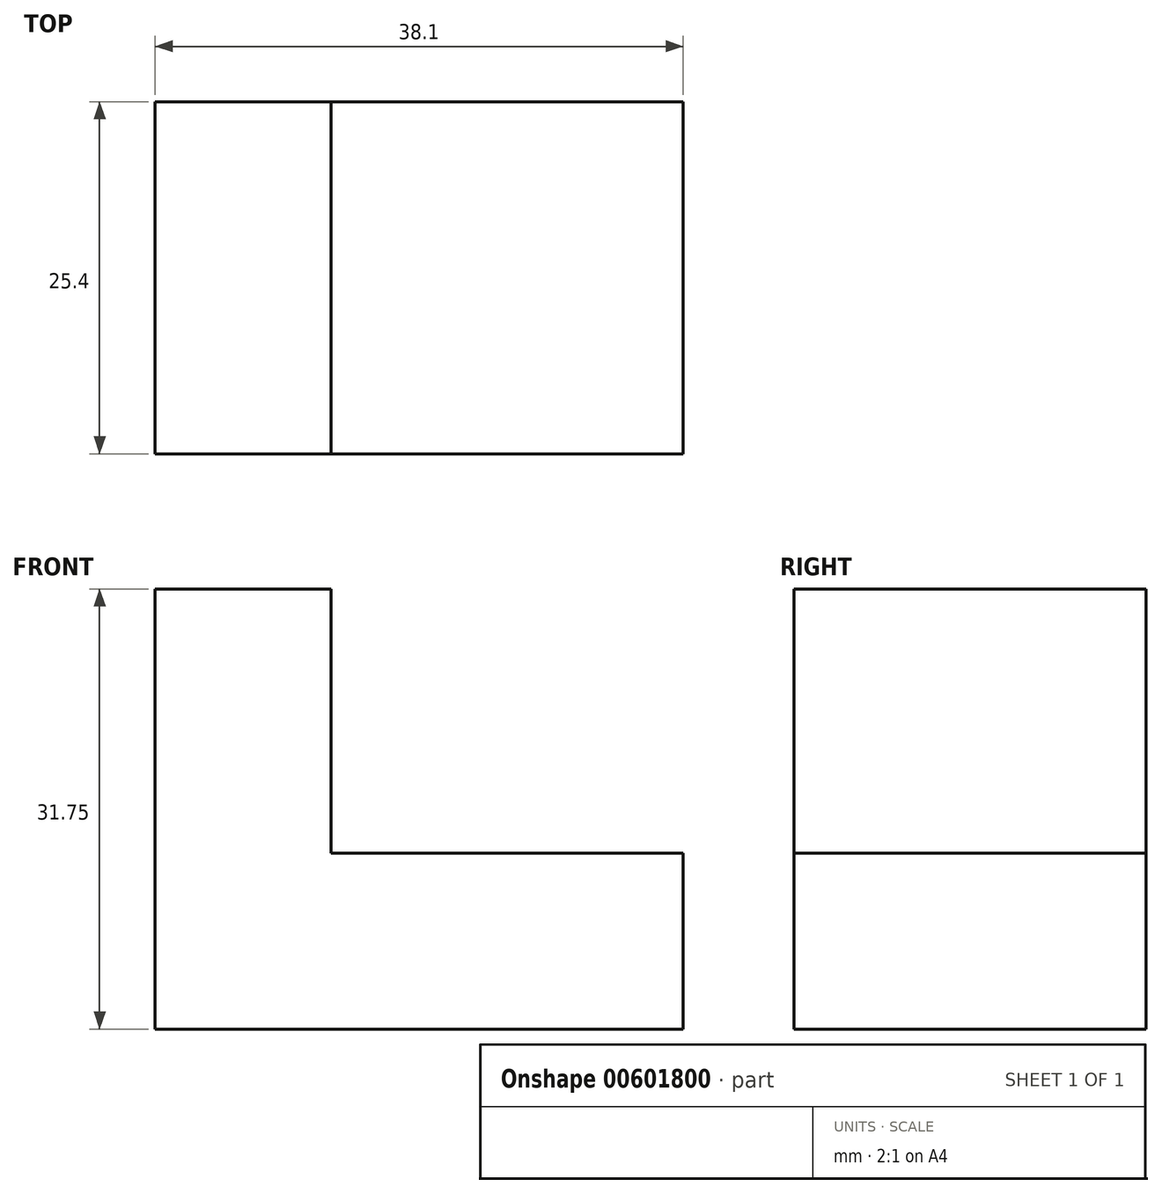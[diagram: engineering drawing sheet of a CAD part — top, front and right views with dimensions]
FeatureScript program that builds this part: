
annotation { "Feature Type Name" : "Feature", "Feature Type Description" : "" }
export const myFeature = defineFeature(function(context is Context, id is Id, definition is map)
    precondition{}
    {
        {
            var Q0;
            Q0=qCreatedBy(makeId("Front.planeOp"),FACE);
            var sketch = newSketch(context, id + "F0", { "sketchPlane" : qUnion([Q0])});
            skLineSegment(sketch, "E0", {"start": v(0, 0) * mm, "end": v(0, 31.75) * mm});
            skLineSegment(sketch, "E1", {"start": v(0, 31.75) * mm, "end": v(12.7, 31.75) * mm});
            skLineSegment(sketch, "E2", {"start": v(12.7, 31.75) * mm, "end": v(12.7, 12.7) * mm});
            skLineSegment(sketch, "E3", {"start": v(12.7, 12.7) * mm, "end": v(38.1, 12.7) * mm});
            skLineSegment(sketch, "E4", {"start": v(38.1, 12.7) * mm, "end": v(38.1, 0) * mm});
            skLineSegment(sketch, "E5", {"start": v(38.1, 0) * mm, "end": v(-7.5, 0) * mm});
            skSolve(sketch);
        }
        {
            var Q0;
            Q0 = qSketchRegion(id + "F0", true);
            extrude(context, id + "F1", {"entities" : qUnion([Q0]), "depth" : 25.4 * mm, "offsetDistance" : 25.4 * mm});
        }
    });
